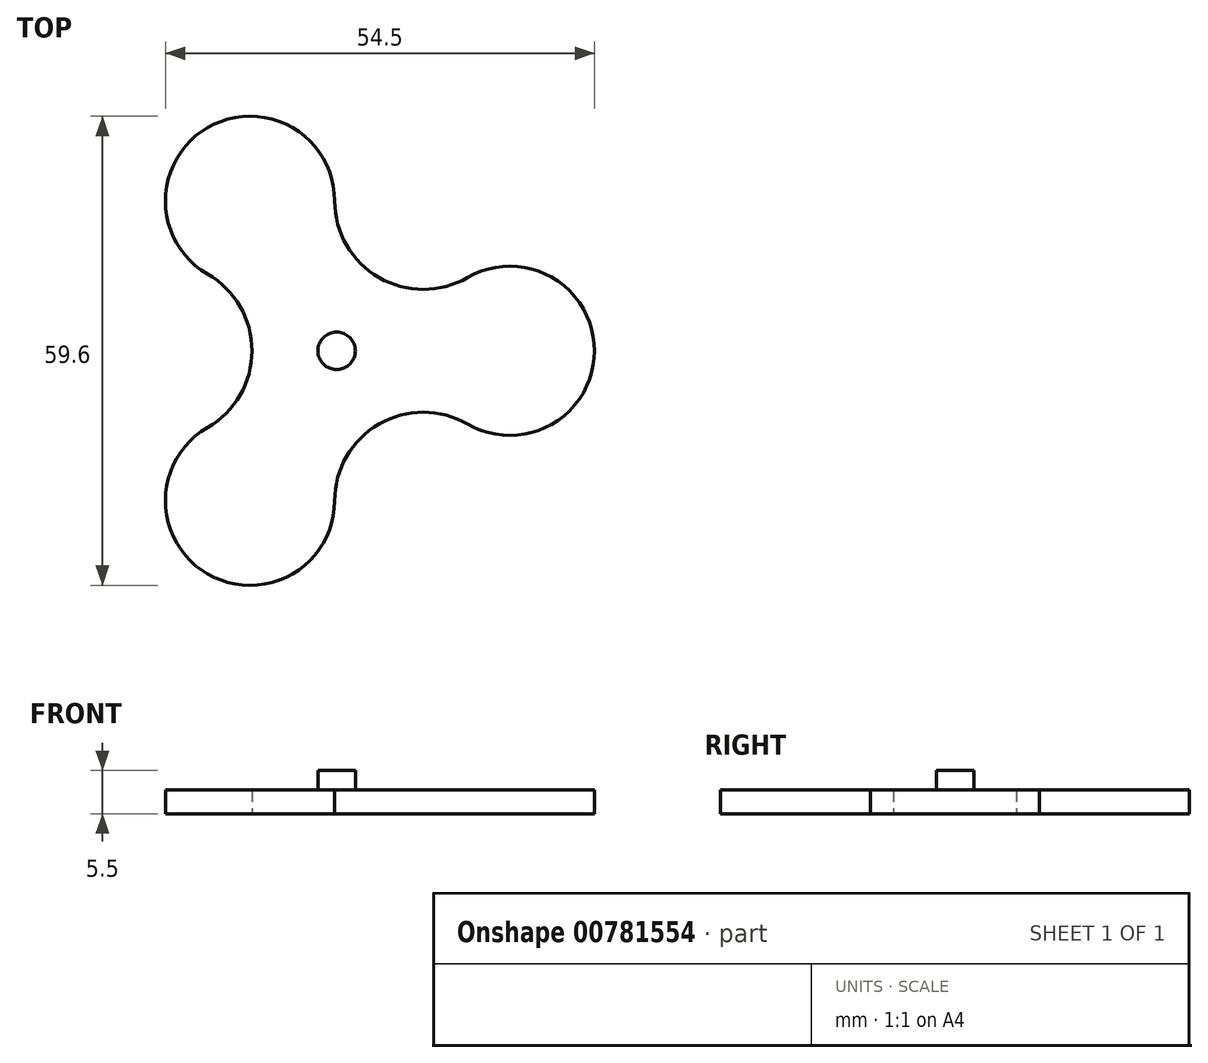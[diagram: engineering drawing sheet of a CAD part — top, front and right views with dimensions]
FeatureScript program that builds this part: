
annotation { "Feature Type Name" : "Feature", "Feature Type Description" : "" }
export const myFeature = defineFeature(function(context is Context, id is Id, definition is map)
    precondition{}
    {
        {
            var Q0;
            Q0=qCreatedBy(makeId("Top.planeOp"),FACE);
            var sketch = newSketch(context, id + "F0", { "sketchPlane" : qUnion([Q0])});
            skArc(sketch, "E0.0.0", {"start": v(16.62, 9.3) * mm, "mid": v(32.75, 0) * mm, "end": v(16.62, -9.3) * mm});
            skArc(sketch, "E0.0.1", {"start": v(16.62, 9.3) * mm, "mid": v(5.37, 9.3) * mm, "end": v(-0.25, 19.05) * mm});
            skArc(sketch, "E0.0.2", {"start": v(-0.25, 19.05) * mm, "mid": v(-16.37, 28.36) * mm, "end": v(-16.38, 9.74) * mm});
            skArc(sketch, "E0.0.3", {"start": v(-16.38, 9.74) * mm, "mid": v(-10.75, 0) * mm, "end": v(-16.38, -9.74) * mm});
            skArc(sketch, "E0.0.4", {"start": v(-16.38, -9.74) * mm, "mid": v(-16.38, -28.36) * mm, "end": v(-0.25, -19.05) * mm});
            skArc(sketch, "E0.0.5", {"start": v(-0.25, -19.05) * mm, "mid": v(5.37, -9.3) * mm, "end": v(16.62, -9.3) * mm});
            skCircle(sketch, "E1", {"center": v(0, 0) * mm, "radius": 22 * mm, "construction": true});
            skLineSegment(sketch, "E2", {"start": v(-11, 19.05) * mm, "end": v(0, 0) * mm, "construction": true});
            skLineSegment(sketch, "E3", {"start": v(0, 0) * mm, "end": v(22, 0) * mm, "construction": true});
            skCircle(sketch, "E4", {"center": v(0, 0) * mm, "radius": 32.75 * mm, "construction": true});
            skSolve(sketch);
        }
        {
            var Q0;
            Q0 = qSketchRegion(id + "F0", true);
            extrude(context, id + "F1", {"entities" : qUnion([Q0]), "depth" : 3 * mm, "offsetDistance" : 25 * mm});
        }
        {
            var Q0;
            Q0=makeQuery(id+"F1.opExtrude","CAP_FACE",FACE,{"disambiguationData":[OSD([sQuery(id+"F0.wireOp",EDGE,"E0.0.0"),sQuery(id+"F0.wireOp",EDGE,"E0.0.1"),sQuery(id+"F0.wireOp",EDGE,"E0.0.2"),sQuery(id+"F0.wireOp",EDGE,"E0.0.3"),sQuery(id+"F0.wireOp",EDGE,"E0.0.4"),sQuery(id+"F0.wireOp",EDGE,"E0.0.5")])],"isStart":false});
            var sketch = newSketch(context, id + "F2", { "sketchPlane" : qUnion([Q0])});
            skCircle(sketch, "E5", {"center": v(0, 0) * mm, "radius": 2.38 * mm});
            skSolve(sketch);
        }
        {
            var Q0;
            Q0 = qSketchRegion(id + "F2", true);
            extrude(context, id + "F3", {"entities" : qUnion([Q0]), "operationType" : NewBodyOperationType.ADD, "depth" : 2.5 * mm, "offsetDistance" : 25 * mm});
        }
    });
